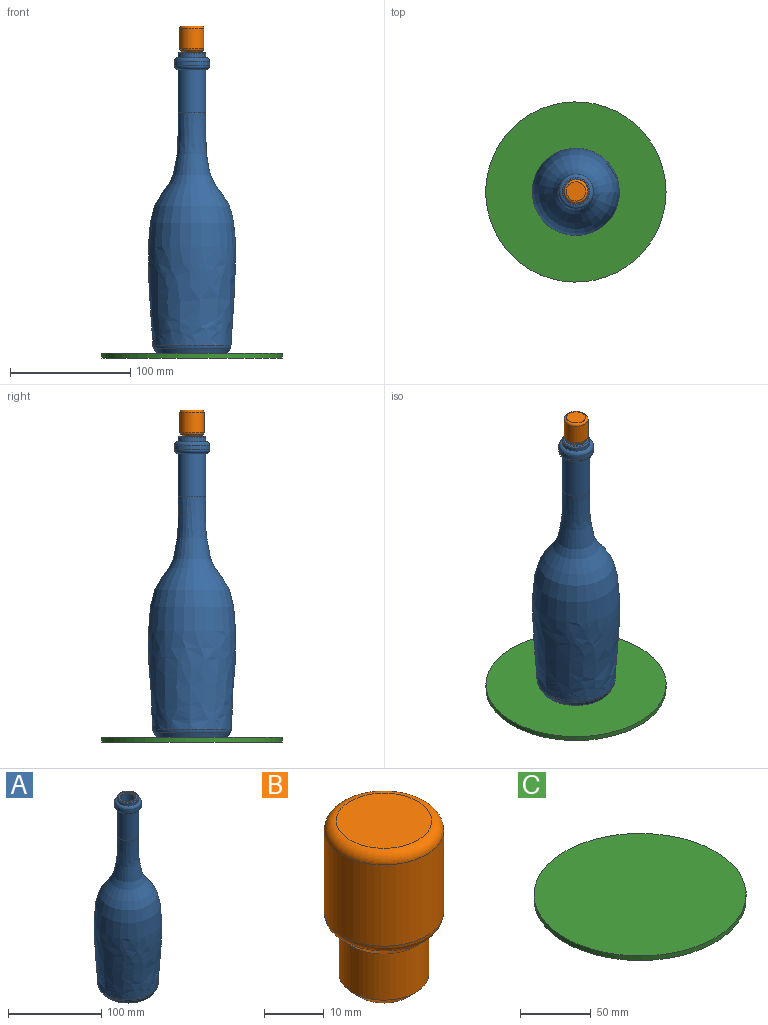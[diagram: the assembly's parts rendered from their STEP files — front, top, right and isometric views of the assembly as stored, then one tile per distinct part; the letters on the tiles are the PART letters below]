
ASSEMBLY  parts=3 mates=3
PART A: 17 faces, bbox 72.7x72.7x250 mm
  f0: cylinder r=3mm len=14.15mm, axis (0,0,1), area 266.7mm2, adj f1,f16
  f1: plane 6x6mm, normal (0,0,-1), area 28.3mm2, adj f0
  f2: plane 15x15mm, normal (0,0,1), area 176.7mm2, adj f3
  f3: cylinder r=7.5mm len=134.79mm, axis (0,0,1), area 6351.6mm2, adj f2,f4
  f4: torus R=8.5mm, axis (0,0,1), area 77.6mm2, adj f3,f5
  f5: plane 21x21mm, normal (0,0,1), area 119.4mm2, adj f4,f6
  f6: torus R=10.5mm, axis (0,0,1), area 109.9mm2, adj f5,f7
  f7: cylinder r=11.5mm len=23mm, axis (0,0,1), area 216.8mm2, adj f6,f8
  f8: torus R=11.5mm, axis (0,0,1), area 397.1mm2, adj f7,f9
  f9: cylinder r=14.5mm len=29mm, axis (0,0,1), area 364.4mm2, adj f8,f10
  f10: torus R=11.5mm, axis (0,0,1), area 397.1mm2, adj f9,f11
  f11: cylinder r=11.5mm len=36mm, axis (0,0,1), area 2601.2mm2, adj f10,f12
  f12: revolved ~193.93x72.69mm, area 34036.8mm2, adj f11,f13
  f13: torus R=27.52mm, axis (0,0,1), area 441mm2, adj f12,f14
  f14: cone r=30mm half-angle=26.6deg, axis (0,0,1), area 867.8mm2, adj f13,f15
  f15: plane 60x60mm, normal (0,0,-1), area 2748.9mm2, adj f14,f16
  f16: cone r=5mm half-angle=45deg, axis (0,0,-1), area 71.1mm2, adj f0,f15
PART B: 8 faces, bbox 21.6x21.6x33.5 mm
  f0: plane 11x11mm, normal (0,0,-1), area 95mm2, adj f4
  f1: plane 16x16mm, normal (0,0,1), area 201.1mm2, adj f6
  f2: cylinder r=10mm len=20mm, axis (0,0,1), area 1047.9mm2, adj f6,f7
  f3: cylinder r=7.5mm len=15mm, axis (0,0,1), area 448.8mm2, adj f4,f5
  f4: cone r=7.5mm half-angle=45deg, axis (0,0,1), area 115.5mm2, adj f0,f3
  f5: cone r=9.5mm half-angle=45deg, axis (0,0,1), area 151.1mm2, adj f3,f7
  f6: torus R=8mm, axis (0,0,-1), area 183mm2, adj f1,f2
  f7: torus R=8mm, axis (0,0,-1), area 89.3mm2, adj f2,f5
PART C: 3 faces, bbox 150x150x4 mm
  f0: cylinder r=75mm len=150mm, axis (0,0,-1), area 1885mm2, adj f1,f2
  f1: plane 150x150mm, normal (0,0,1), area 17671.5mm2, adj f0
  f2: plane 150x150mm, normal (0,0,-1), area 17671.5mm2, adj f0
PLACE A t=(0,0,-214)mm
PLACE B t=(0,0,38.27)mm
PLACE C t=(0,0,-218)mm
MATE planar C.f0 <-> A.f0  axis (0,0,1) through (0,0,-214)mm
MATE cylindrical B.f2 <-> A.f0  axis (0,0,1) through (0,0,47.93)mm
MATE cylindrical A.f0 <-> C.f0  axis (0,0,1) through (0,0,4)mm
